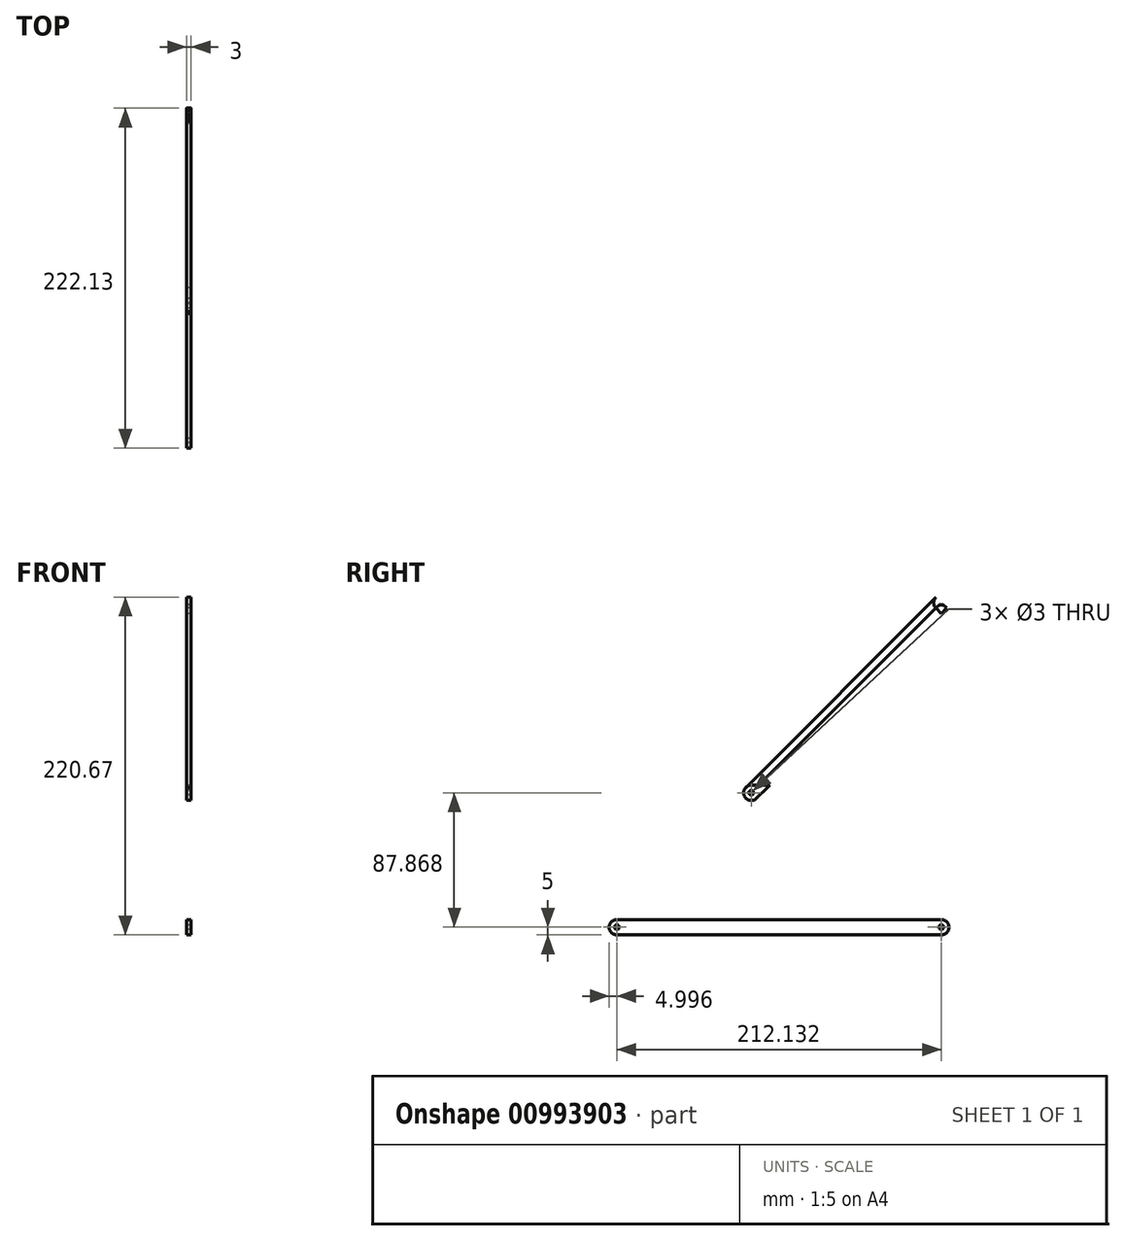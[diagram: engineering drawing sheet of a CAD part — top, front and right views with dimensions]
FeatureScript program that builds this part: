
annotation { "Feature Type Name" : "Feature", "Feature Type Description" : "" }
export const myFeature = defineFeature(function(context is Context, id is Id, definition is map)
    precondition{}
    {
        {
            var Q0;
            Q0=qCreatedBy(makeId("Right.planeOp"),FACE);
            var sketch = newSketch(context, id + "F0", { "sketchPlane" : qUnion([Q0])});
            skLineSegment(sketch, "E0", {"start": v(0, 0) * mm, "end": v(-212.13, 212.13) * mm});
            skArc(sketch, "E1.0.startCap", {"start": v(3.54, 3.54) * mm, "mid": v(3.54, -3.54) * mm, "end": v(-3.54, -3.54) * mm});
            skArc(sketch, "E1.0.endCap", {"start": v(-215.67, 208.6) * mm, "mid": v(-215.67, 215.67) * mm, "end": v(-208.6, 215.67) * mm});
            skLineSegment(sketch, "E1.0.left", {"start": v(-3.54, -3.54) * mm, "end": v(-215.67, 208.6) * mm});
            skLineSegment(sketch, "E1.0.right", {"start": v(3.54, 3.54) * mm, "end": v(-208.6, 215.67) * mm});
            skLineSegment(sketch, "E2", {"start": v(-212.13, 212.13) * mm, "end": v(-424.26, 0) * mm});
            skArc(sketch, "E3.0.startCap", {"start": v(-215.67, 215.67) * mm, "mid": v(-208.6, 215.67) * mm, "end": v(-208.6, 208.6) * mm});
            skArc(sketch, "E3.0.endCap", {"start": v(-420.73, -3.54) * mm, "mid": v(-427.8, -3.54) * mm, "end": v(-427.8, 3.54) * mm});
            skLineSegment(sketch, "E3.0.left", {"start": v(-208.6, 208.6) * mm, "end": v(-420.73, -3.54) * mm});
            skLineSegment(sketch, "E3.0.right", {"start": v(-215.67, 215.67) * mm, "end": v(-427.8, 3.54) * mm});
            skLineSegment(sketch, "E4", {"start": v(0, 0) * mm, "end": v(230.96, 0) * mm, "construction": true});
            skLineSegment(sketch, "E5", {"start": v(-212.13, 0) * mm, "end": v(-424.26, 0) * mm});
            skArc(sketch, "E6.0.startCap", {"start": v(-212.13, 5) * mm, "mid": v(-207.13, 0) * mm, "end": v(-212.13, -5) * mm});
            skArc(sketch, "E6.0.endCap", {"start": v(-424.26, -5) * mm, "mid": v(-429.26, 0) * mm, "end": v(-424.26, 5) * mm});
            skLineSegment(sketch, "E6.0.left", {"start": v(-212.13, -5) * mm, "end": v(-424.26, -5) * mm});
            skLineSegment(sketch, "E6.0.right", {"start": v(-212.13, 5) * mm, "end": v(-424.26, 5) * mm});
            skLineSegment(sketch, "E7", {"start": v(-212.13, 212.13) * mm, "end": v(-212.13, -75.06) * mm, "construction": true});
            skLineSegment(sketch, "E8", {"start": v(0, 0) * mm, "end": v(0, 300) * mm, "construction": true});
            skArc(sketch, "E9", {"start": v(0, 0) * mm, "mid": v(-136.58, 32.9) * mm, "end": v(-243.21, 124.37) * mm, "construction": true});
            skLineSegment(sketch, "E10", {"start": v(-212.13, 87.87) * mm, "end": v(-336.4, 87.87) * mm});
            skArc(sketch, "E11.0.startCap", {"start": v(-212.13, 92.87) * mm, "mid": v(-207.13, 87.87) * mm, "end": v(-212.13, 82.87) * mm});
            skArc(sketch, "E11.0.endCap", {"start": v(-336.4, 82.87) * mm, "mid": v(-341.4, 87.87) * mm, "end": v(-336.4, 92.87) * mm});
            skLineSegment(sketch, "E11.0.left", {"start": v(-212.13, 82.87) * mm, "end": v(-336.4, 82.87) * mm});
            skLineSegment(sketch, "E11.0.right", {"start": v(-212.13, 92.87) * mm, "end": v(-336.4, 92.87) * mm});
            skLineSegment(sketch, "E12", {"start": v(-212.13, 87.87) * mm, "end": v(-87.87, 87.87) * mm, "construction": true});
            skSolve(sketch);
        }
        {
            var Q0;
            Q0=makeQuery(id+"F0.imprint","IMPRINT",FACE,{"disambiguationData":[TD([[makeQuery(id+"F0.imprint","IMPRINT",EDGE,{"derivedFrom":sQuery(id+"F0.wireOp",EDGE,"E1.0.startCap")}),-1.0]])]});
            var Q1;
            {var subQ0=sQuery(id+"F0.wireOp",EDGE,"E2");var subQ1=sQuery(id+"F0.wireOp",EDGE,"E0");var subQ2=makeQuery(id+"F0.imprint","INTERSECT",VERTEX,{"derivedFrom":[subQ1,subQ0]});Q1=makeQuery(id+"F0.imprint","IMPRINT",FACE,{"disambiguationData":[TD([[makeQuery(id+"F0.imprint","IMPRINT",EDGE,{"disambiguationData":[TD([[subQ2,1.0]])],"derivedFrom":subQ1}),1.0]])]});}
            var Q2;
            {var subQ3=sQuery(id+"F0.wireOp",EDGE,"E1.0.endCap");Q2=makeQuery(id+"F0.imprint","IMPRINT",FACE,{"disambiguationData":[TD([[makeQuery(id+"F0.imprint","IMPRINT",EDGE,{"derivedFrom":subQ3}),-1.0]])]});}
            extrude(context, id + "F1", {"entities" : qUnion([Q0, Q1, Q2]), "depth" : 3 * mm, "offsetDistance" : 25 * mm});
        }
        {
            var Q0;
            {var subQ2=sQuery(id+"F0.wireOp",EDGE,"E3.0.endCap");Q0=makeQuery(id+"F0.imprint","IMPRINT",FACE,{"disambiguationData":[TD([[makeQuery(id+"F0.imprint","IMPRINT",EDGE,{"derivedFrom":subQ2}),1.0]])]});}
            var Q1;
            {var subQ0=sQuery(id+"F0.wireOp",EDGE,"E5");var subQ1=sQuery(id+"F0.wireOp",EDGE,"E2");var subQ2=makeQuery(id+"F0.imprint","INTERSECT",VERTEX,{"derivedFrom":[subQ1,subQ0]});Q1=makeQuery(id+"F0.imprint","IMPRINT",FACE,{"disambiguationData":[TD([[makeQuery(id+"F0.imprint","IMPRINT",EDGE,{"disambiguationData":[TD([[subQ2,1.0]])],"derivedFrom":subQ1}),1.0]])]});}
            var Q2;
            {var subQ5=sQuery(id+"F0.wireOp",EDGE,"E3.0.endCap");Q2=makeQuery(id+"F0.imprint","IMPRINT",FACE,{"disambiguationData":[TD([[makeQuery(id+"F0.imprint","IMPRINT",EDGE,{"derivedFrom":subQ5}),-1.0]])]});}
            extrude(context, id + "F2", {"entities" : qUnion([Q0, Q1, Q2]), "depth" : 3 * mm, "offsetDistance" : 25 * mm});
        }
        {
            var Q0;
            Q0=sQuery(id+"F0.wireOp",VERTEX,"E5.start");
            var Q1;
            Q1=sQuery(id+"F0.wireOp",VERTEX,"E2.end");
            var Q2;
            Q2=sQuery(id+"F0.wireOp",VERTEX,"E0.start");
            var Q3;
            Q3=sQuery(id+"F0.wireOp",VERTEX,"E0.end");
            var Q4;
            Q4=makeQuery(id+"F1.opExtrude","SWEPT_BODY",BODY,{"disambiguationData":[OSD([sQuery(id+"F0.wireOp",EDGE,"E1.0.startCap"),sQuery(id+"F0.wireOp",EDGE,"E1.0.endCap"),sQuery(id+"F0.wireOp",EDGE,"E1.0.left"),sQuery(id+"F0.wireOp",EDGE,"E1.0.right"),sQuery(id+"F0.wireOp",EDGE,"E3.0.startCap")])]});
            var Q5;
            Q5=makeQuery(id+"F2.opExtrude","SWEPT_BODY",BODY,{"disambiguationData":[OSD([sQuery(id+"F0.wireOp",EDGE,"E6.0.startCap"),sQuery(id+"F0.wireOp",EDGE,"E6.0.endCap"),sQuery(id+"F0.wireOp",EDGE,"E6.0.left"),sQuery(id+"F0.wireOp",EDGE,"E6.0.right")])]});
            hole(context, id + "F3", {"style" : HoleStyle.SIMPLE, "endStyle" : HoleEndStyle.THROUGH, "oppositeDirection" : true, "holeDiameter" : 3 * mm, "majorDiameter" : 5 * mm, "isTappedThrough" : true, "tappedDepth" : 12 * mm, "tapClearance" : 3, "locations" : qUnion([Q0, Q1, Q2, Q3]), "scope" : qUnion([Q4, Q5])});
        }
        {
            var Q0;
            {var subQ0=sQuery(id+"F0.wireOp",EDGE,"E11.0.startCap");Q0=makeQuery(id+"F0.imprint","IMPRINT",FACE,{"disambiguationData":[TD([[makeQuery(id+"F0.imprint","IMPRINT",EDGE,{"derivedFrom":subQ0}),-1.0]])]});}
            var Q1;
            {var subQ0=sQuery(id+"F0.wireOp",EDGE,"E10");var subQ1=sQuery(id+"F0.wireOp",EDGE,"E2");var subQ2=makeQuery(id+"F0.imprint","INTERSECT",VERTEX,{"derivedFrom":[subQ1,subQ0]});Q1=makeQuery(id+"F0.imprint","IMPRINT",FACE,{"disambiguationData":[TD([[makeQuery(id+"F0.imprint","IMPRINT",EDGE,{"disambiguationData":[TD([[subQ2,1.0]])],"derivedFrom":subQ1}),1.0]])]});}
            var Q2;
            {var subQ4=sQuery(id+"F0.wireOp",EDGE,"E2");var subQ6=makeQuery(id+"F0.imprint","INTERSECT",VERTEX,{"derivedFrom":[subQ4,sQuery(id+"F0.wireOp",EDGE,"E10")]});Q2=makeQuery(id+"F0.imprint","IMPRINT",FACE,{"disambiguationData":[TD([[makeQuery(id+"F0.imprint","IMPRINT",EDGE,{"disambiguationData":[TD([[subQ6,1.0]])],"derivedFrom":subQ4}),-1.0]])]});}
            var Q3;
            {var subQ0=sQuery(id+"F0.wireOp",EDGE,"E10");var subQ1=sQuery(id+"F0.wireOp",EDGE,"E2");var subQ2=makeQuery(id+"F0.imprint","INTERSECT",VERTEX,{"derivedFrom":[subQ1,subQ0]});Q3=makeQuery(id+"F0.imprint","IMPRINT",FACE,{"disambiguationData":[TD([[makeQuery(id+"F0.imprint","IMPRINT",EDGE,{"disambiguationData":[TD([[subQ2,-1.0]])],"derivedFrom":subQ1}),1.0]])]});}
            extrude(context, id + "F4", {"entities" : qUnion([Q0, Q1, Q2, Q3]), "depth" : 3 * mm, "offsetDistance" : 25 * mm});
        }
        {
            var Q0;
            Q0=sQuery(id+"F0.wireOp",VERTEX,"E10.end");
            var Q1;
            Q1=sQuery(id+"F0.wireOp",VERTEX,"E10.start");
            var Q2;
            Q2=makeQuery(id+"F4.opExtrude","SWEPT_BODY",BODY,{"disambiguationData":[OSD([sQuery(id+"F0.wireOp",EDGE,"E11.0.startCap"),sQuery(id+"F0.wireOp",EDGE,"E11.0.endCap"),sQuery(id+"F0.wireOp",EDGE,"E11.0.left"),sQuery(id+"F0.wireOp",EDGE,"E11.0.right")])]});
            hole(context, id + "F5", {"style" : HoleStyle.SIMPLE, "endStyle" : HoleEndStyle.THROUGH, "oppositeDirection" : true, "holeDiameter" : 3 * mm, "majorDiameter" : 5 * mm, "isTappedThrough" : true, "tappedDepth" : 12 * mm, "tapClearance" : 3, "locations" : qUnion([Q0, Q1]), "scope" : qUnion([Q2])});
        }
        {
            var Q0;
            Q0=sQuery(id+"F0.wireOp",VERTEX,"E12.end");
            var Q1;
            Q1=makeQuery(id+"F1.opExtrude","SWEPT_BODY",BODY,{"disambiguationData":[OSD([sQuery(id+"F0.wireOp",EDGE,"E1.0.startCap"),sQuery(id+"F0.wireOp",EDGE,"E1.0.endCap"),sQuery(id+"F0.wireOp",EDGE,"E1.0.left"),sQuery(id+"F0.wireOp",EDGE,"E1.0.right"),sQuery(id+"F0.wireOp",EDGE,"E3.0.startCap")])]});
            hole(context, id + "F6", {"style" : HoleStyle.SIMPLE, "endStyle" : HoleEndStyle.THROUGH, "oppositeDirection" : true, "holeDiameter" : 3 * mm, "majorDiameter" : 5 * mm, "isTappedThrough" : true, "tappedDepth" : 12 * mm, "tapClearance" : 3, "locations" : qUnion([Q0]), "scope" : qUnion([Q1])});
        }
    });
